# Revit family: PRD_AR_ShwrFttngsPckg_F5EElectronicShowerFitting_F5EV2006
name_source: partatom
category: Plumbing Fixtures
units: mm (PartAtom-declared; Revit-internal decimal feet)

## family parameters
Cut with Voids When Loaded = Yes
Enable Cutting in Views = Yes
Host = Face
Maintain Annotation Orientation = No
OmniClass Number = 23.45.05.14.99
OmniClass Title = Other Sanitary Washing Plumbing Fixtures
Part Type = Normal
Room Calculation Point = No
Round Connector Dimension = Use Diameter
Shared = No

## types (1)
- F5EV2006
    AdditionalConnections = No
    AdjustableFlowTime = Yes
    AssetType = Fixed
    BIMObjectName = PRD_AR_ ShowerFittingsPackage_F5EElectronicShowerFitting_F5EV2006
    BasicColour = stainless steel-look
    BodyMaterial = PRD_AR_StainlessSteel_Brushed
    BuiltInFittingModel = Built-in section
    ButtonMaterial = PRD_AR_ChromatedBrass_HighPolished
    CW Connection = Yes
    CWFU = 0
    Category = Pr_40_20_87_75, Shower fittings package
    Circulation = No
    Color = stainless steel-look
    CompatibleA3000Open = Yes
    ConnectionWithPayWaterDispenser = single / multiple pay water dispenser
    CoverPlateHeight = 245 mm
    CoverPlateWidth = 190 mm
    Default Elevation = 1219 mm
    DefaultAutomaticHygieneFlush = 24h after the last activity
    DefaultFlowTime = 30 Seconds
    Description = F5E - A3000 open straight-way valve DN 15 for shower facilities, for concealed mounting. Especially suitable for facilities at risk of vandalism. Electronically controlled, for connection to pre-mixed hot water or cold water. With waterproof electronic module and electric T-junction for connection to system cable, solenoid valve, 190 x 245 x 2 mm stainless steel cover plate for invisible mounting via threaded rods, up to a wall thickness of 50 to 500 mm, including piezo push-button with start/stop function and 2 m extension cable. Connection and maintenance via service room. Activated hygiene flushing 24 hours after the last activity. With facility for parameterization, cleaning deactivation and communication via ECC2 function controller, 24 V DC.
    DiameterNominal = DN 15
    DrainSize = 15 mm  [stored 0.0492126 ft]
    Export Type to IFC As = IfcSanitaryTerminalType
    Features = Electronically controlled, for connection to pre-mixed hotwater or cold water. 190 x 245x 2 mm stainless steel cover plate for invisible mounting viathreaded rods, up to a wall thickness of 50 to 500 mm.
    Finish = Satin finished
    FunctionalPrinciple = electronic self-closing
    HW Connection = Yes
    HWFU = 0
    HasTray = No
    HygieneFlushing = Yes
    IfcExportAs = IfcSanitaryTerminalType
    IfcExportType = SHOWER
    InletSize = G 3/4 B
    LockingMechanism = Top section, non-ceramic
    Manufacturer = KWC Group Management AG
    ManufacturerName = KWC Group Management AG
    ManufacturerURL = www.kwc-professional.com
    Material = stainless steel
    MaterialCasing = stainless steel
    MaterialCodeCasing = 1.4301 Chrome Nickel steel V2A
    MaximumFlowTime = 255 Seconds
    MinimumFlowPressure = 1 bar
    MinimumFlowTime = 1 Seconds
    Model = F5EV2006
    ModelNumber = 2030068173
    ModelReference = F5EV2006
    NBSDescription = Shower fittings package
    NBSReference = 45-35-70/330
    Name = F5E Electronic shower fitting F5EV2006
    NominalDepth = 2 mm  [stored 0.00656168 ft]
    NominalHeight = 245 mm
    NominalLength = 245 mm
    NominalWidth = 190 mm
    Parameterization = network
    PowerSupplyConnection = A3000 open 24 V DC
    ProductInformation = http://pim.kwc.com
    ProtectiveShutdown = Yes
    ProtectiveSystemIP = IP59K
    ShowerHead = without shower head
    ShowerPipeDraining = No
    ShowerType = Individual
    Size = 15
    SoundInsulation = No
    Status = NEW
    SurfaceFinishCasing = satin finished
    TemperatureLimit = No
    Type IFC Predefined Type = USERDEFINED
    TypeOfMixing = No
    TypeOfMounting = bolt mounting
    TypeOfOperation = sensor operation
    TypeOfPowerSupply = Transformer
    TypeOfSensor = piezo-electronic sensor
    TypeOfShower = in-wall fitting
    URL = www.kwc-professional.com
    Uniclass2015Code = Pr_40_20_87_75
    Uniclass2015Title = Shower fittings package
    Uniclass2015Version = Products v1.36
    Vent Connection = Yes
    Version = 1
    VolumeFlowRateAt3Bar = 0.47 l/s
    WFU = 0
    Waste Connection = Yes
    WaterConnection = pipe
    WithBackflowPreventer = No
    WithFilter = Yes
    WithRosettesCoverPlate = Yes
    WithSoapDish = No
    WithTransformerPowerSupply = No

note: [stored X ft] marks values corroborated as IEEE doubles in the binary element streams (Revit-internal decimal feet)

## geometry (parser evidence)
native form markers: Sweep x7
no freeform markers — native parametric forms only
